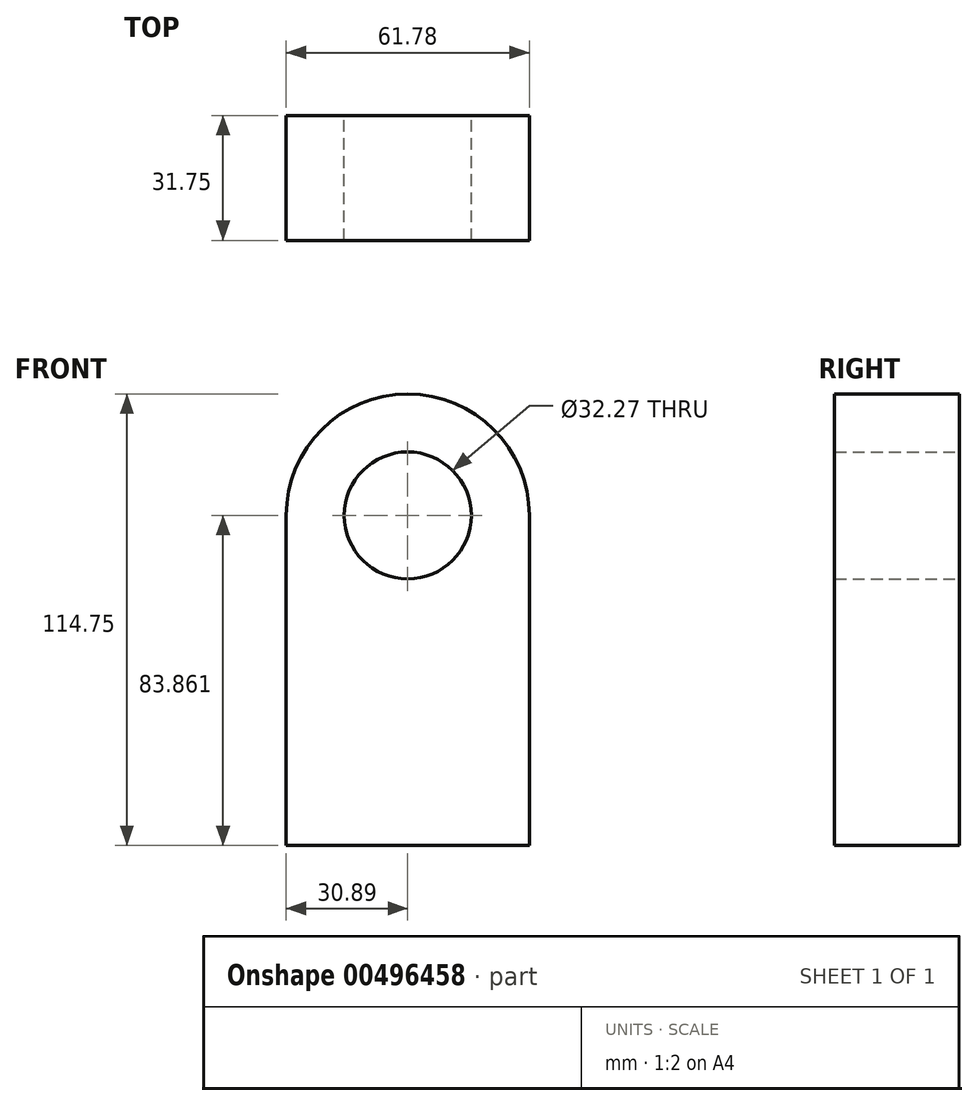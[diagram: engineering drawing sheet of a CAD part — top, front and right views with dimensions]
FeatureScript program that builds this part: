
annotation { "Feature Type Name" : "Feature", "Feature Type Description" : "" }
export const myFeature = defineFeature(function(context is Context, id is Id, definition is map)
    precondition{}
    {
        {
            var Q0;
            Q0=qCreatedBy(makeId("Front.planeOp"),FACE);
            var sketch = newSketch(context, id + "F0", { "sketchPlane" : qUnion([Q0])});
            skLineSegment(sketch, "E0.top", {"start": v(30.89, -41.93) * mm, "end": v(-30.89, -41.93) * mm});
            skLineSegment(sketch, "E0.left", {"start": v(30.89, 41.93) * mm, "end": v(30.89, -41.93) * mm});
            skLineSegment(sketch, "E0.right", {"start": v(-30.89, 41.93) * mm, "end": v(-30.89, -41.93) * mm});
            skPoint(sketch, "E0.middle", {"position": v(0, 0) * mm});
            skArc(sketch, "E1", {"start": v(30.89, 41.93) * mm, "mid": v(0, 72.82) * mm, "end": v(-30.89, 41.93) * mm});
            skCircle(sketch, "E2", {"center": v(0, 41.93) * mm, "radius": 16.13 * mm});
            skSolve(sketch);
        }
        {
            var Q0;
            Q0=makeQuery(id+"F0.imprint","IMPRINT",FACE,{"disambiguationData":[TD([[makeQuery(id+"F0.imprint","IMPRINT",EDGE,{"derivedFrom":sQuery(id+"F0.wireOp",EDGE,"E0.top")}),-1.0]])]});
            extrude(context, id + "F1", {"entities" : qUnion([Q0]), "depth" : 31.75 * mm});
        }
    });
